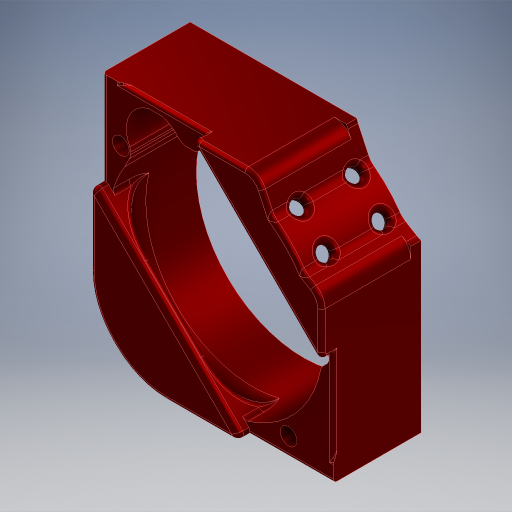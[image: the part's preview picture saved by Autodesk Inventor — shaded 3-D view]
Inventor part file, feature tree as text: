
AUTODESK INVENTOR PART (.ipt)
format: ipt  version: 2024.2 (Build 282272000, 272)  size: 4,193,792 bytes
history: native  units: in
note: dims shown in document units (in); Inventor stores cm internally (conversion verified against a paired STEP export)
features: extrude x10, sketch x10, fillet x3, projected_geometry x1
ambient origin geometry x8: Origin, YZ Plane, XZ Plane, XY Plane, X Axis, Y Axis, Z Axis, Center Point
bodies: Solid1 (feature_tree)
feature tree (24):
  extrude  "Extrusion1"  Depth=0.3937in TaperAngle=0.0deg
  extrude  "Extrusion2"  Depth=0.0591in TaperAngle=0.0deg
  extrude  "Extrusion3"  Depth=0.3937in
  extrude  "Extrusion4"  Depth=0.2313in TaperAngle=0.0deg
  extrude  "Extrusion5"  Depth=0.0013in
  extrude  "Extrusion6"  Depth=0.0197in
  extrude  "Extrusion7"  Depth=7.0034in TaperAngle=0.0deg
  extrude  "Extrusion8"  Depth=1.9685in
  extrude  "Extrusion9"  [1 undecoded]
  fillet  "Fillet3"  [1 undecoded]
  fillet  "Fillet4"  [1 undecoded]
  extrude  "Extrusion10"  [1 undecoded]
  sketch  "Sketch1"  dims[d0=0.3937in d1=0.0in d2=0.3937in d3=0.0in]
  sketch  "Sketch2"  dims[d4=0.0591in d5=0.0in d8=0.0591in d9=0.0in]
  sketch  "Sketch3"  dims[d11=0.3937in d12=0.0in d13=0.1772in]
  sketch  "Sketch4"  dims[d14=0.2313in d15=0.0in d16=0.2313in d17=0.0in]
  sketch  "Sketch5"  dims[d18=0.2313in d19=0.0in d21=0.0013in]
  sketch  "Sketch6"  dims[d22=0.2313in d23=0.0in d24=0.0197in]
  projected_geometry  "Projected Loop1"
  sketch  "Sketch7"  dims[d25=0.0197in d26=7.0034in d27=0.0in]
  sketch  "Sketch8"  dims[d6=0.0197in d7=1.9685in]
  sketch  "Sketch9"
  sketch  "Sketch10"
  fillet  "Fillet21"  [1 undecoded]
note: 5 required parameter values undecoded (feature->parameter linkage not recoverable at this tier; creation-order binding heuristic only, values carry confidence <= 0.55)
